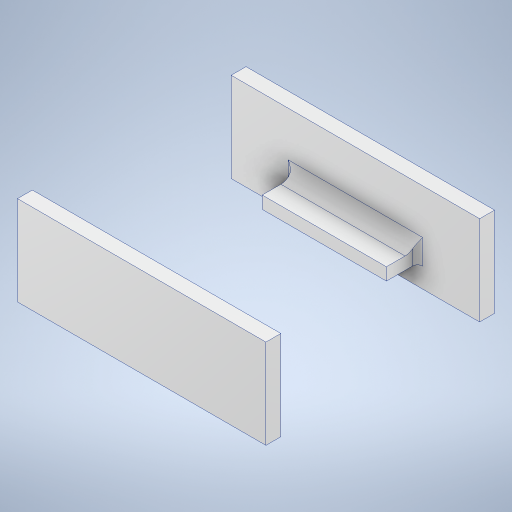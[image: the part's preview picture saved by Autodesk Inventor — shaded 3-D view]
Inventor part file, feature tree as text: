
AUTODESK INVENTOR PART (.ipt)
format: ipt  version: 2024 (Build 280153000, 153)  size: 329,728 bytes
history: native  units: mm
features: extrude x6, sketch x6, projected_geometry x3, fillet x2
ambient origin geometry x8: Origin, YZ Plane, XZ Plane, XY Plane, X Axis, Y Axis, Z Axis, Center Point
bodies: Solid1 (feature_tree)
feature tree (17):
  extrude  "Extrusion1"  Depth=200.0mm
  extrude  "Extrusion2"  Depth=60.0mm
  extrude  "Extrusion3"  Depth=12.0mm
  extrude  "Extrusion6"  Depth=25.0mm TaperAngle=0.0deg
  fillet  "Fillet1"  Radius=12.0mm
  fillet  "Fillet2"  Radius=25.0mm
  extrude  "Extrusion7"  Depth=50.0mm
  extrude  "Extrusion8"  Depth=50.0mm
  sketch  "Sketch1"  dims[d0=160.0mm d1=200.0mm]
  sketch  "Sketch2"  dims[d2=11.0mm d3=0.0mm d4=60.0mm]
  sketch  "Sketch3"  dims[d5=60.0mm d6=12.0mm]
  projected_geometry  "Projected Loop1"
  sketch  "Sketch7"  dims[d7=10.0mm d8=0.0mm d9=5.0mm d10=0.0mm d17=12.0mm d18=25.0mm]
  sketch  "Sketch8"  dims[d19=25.0mm d20=50.0mm]
  sketch  "Sketch10"  dims[d21=50.0mm d22=50.0mm d23=50.0mm d24=10.0mm d25=0.0mm d26=4.0mm d27=10.0mm d28=1000.0mm d29=0.0mm d31=7.0mm d32=0.0mm]
  projected_geometry  "Projected Loop3"
  projected_geometry  "Projected Loop4"
